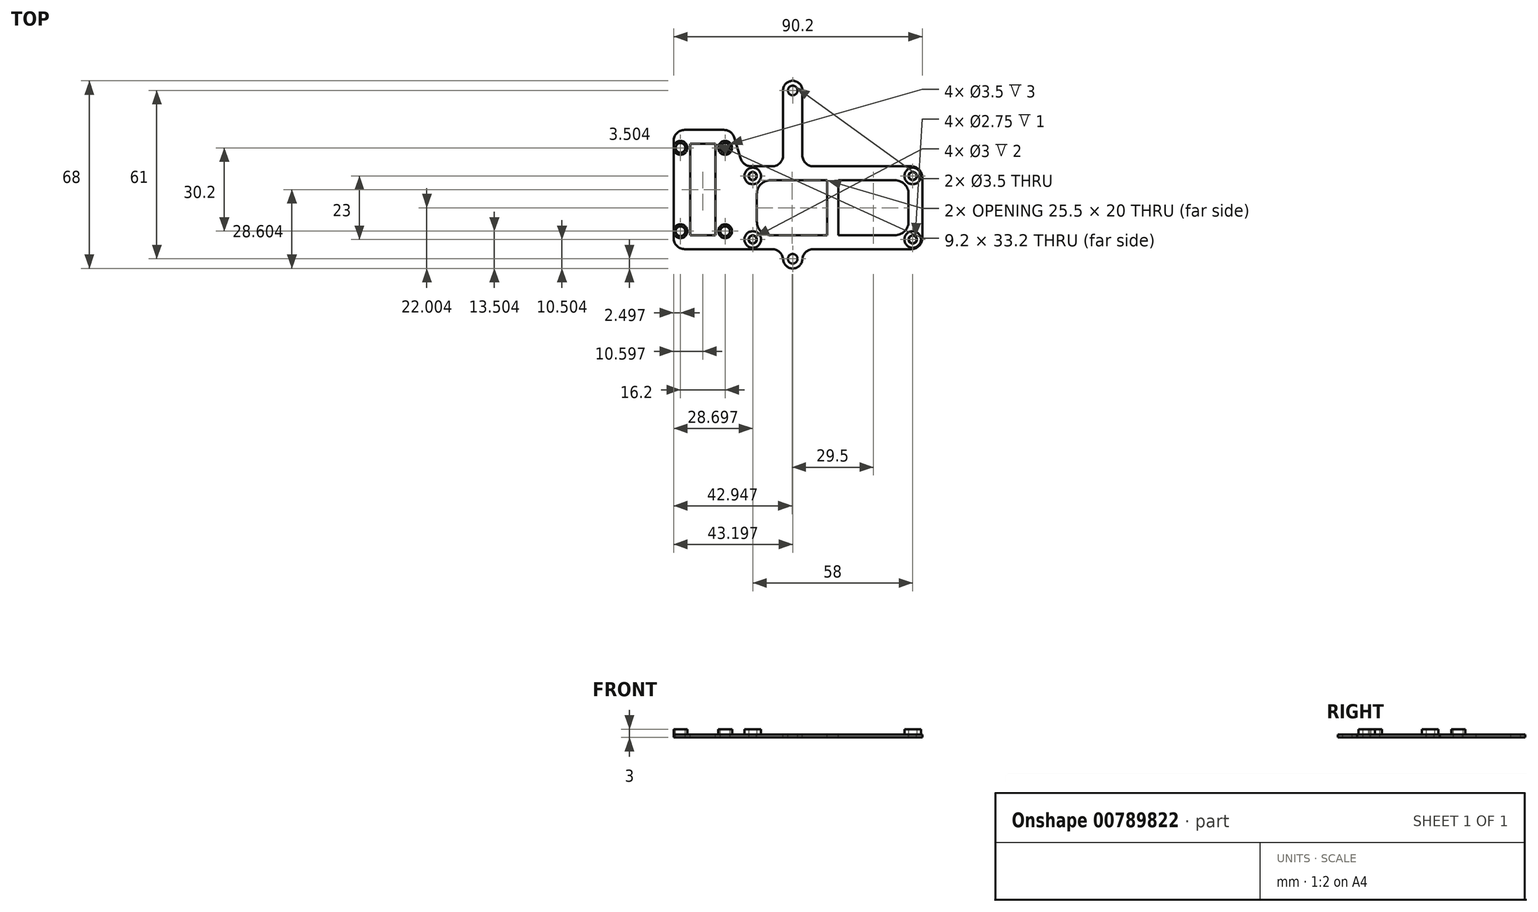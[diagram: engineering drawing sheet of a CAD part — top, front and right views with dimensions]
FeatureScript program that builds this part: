
annotation { "Feature Type Name" : "Feature", "Feature Type Description" : "" }
export const myFeature = defineFeature(function(context is Context, id is Id, definition is map)
    precondition{}
    {
        {
            var Q0;
            Q0=qCreatedBy(makeId("Top.planeOp"),FACE);
            var sketch = newSketch(context, id + "F0", { "sketchPlane" : qUnion([Q0])});
            skLineSegment(sketch, "E0", {"start": v(-80.72, -19.29) * mm, "end": v(-39.23, -19.29) * mm, "construction": true});
            skLineSegment(sketch, "E1", {"start": v(-86.78, -69.8) * mm, "end": v(-86.78, 17.15) * mm, "construction": true});
            skLineSegment(sketch, "E2.bottom", {"start": v(-119.28, -4.29) * mm, "end": v(-54.28, -4.29) * mm});
            skLineSegment(sketch, "E2.top", {"start": v(-119.28, -34.29) * mm, "end": v(-54.28, -34.29) * mm});
            skLineSegment(sketch, "E2.left", {"start": v(-119.28, -4.29) * mm, "end": v(-119.28, -34.29) * mm});
            skLineSegment(sketch, "E2.right", {"start": v(-54.28, -4.29) * mm, "end": v(-54.28, -34.29) * mm});
            skCircle(sketch, "E3", {"center": v(-57.78, -7.79) * mm, "radius": 1.38 * mm});
            skCircle(sketch, "E4.MirrorC", {"center": v(-115.78, -7.79) * mm, "radius": 1.38 * mm});
            skCircle(sketch, "E5.MirrorC", {"center": v(-57.78, -30.79) * mm, "radius": 1.38 * mm});
            skCircle(sketch, "E6.MirrorC", {"center": v(-115.78, -30.79) * mm, "radius": 1.38 * mm});
            skLineSegment(sketch, "E7.bottom", {"start": v(-59.28, -14.29) * mm, "end": v(-59.28, -24.29) * mm});
            skLineSegment(sketch, "E7.top", {"start": v(-84.78, -9.29) * mm, "end": v(-84.78, -29.29) * mm});
            skLineSegment(sketch, "E7.left", {"start": v(-64.28, -9.29) * mm, "end": v(-84.78, -9.29) * mm});
            skLineSegment(sketch, "E7.right", {"start": v(-64.28, -29.29) * mm, "end": v(-84.78, -29.29) * mm});
            skLineSegment(sketch, "E8.MirrorCS", {"start": v(-109.28, -9.29) * mm, "end": v(-88.78, -9.29) * mm});
            skLineSegment(sketch, "E9.MirrorCS", {"start": v(-114.28, -14.29) * mm, "end": v(-114.28, -24.29) * mm});
            skLineSegment(sketch, "E10.MirrorCS", {"start": v(-109.28, -29.29) * mm, "end": v(-88.78, -29.29) * mm});
            skLineSegment(sketch, "E11.MirrorCS", {"start": v(-88.78, -9.29) * mm, "end": v(-88.78, -29.29) * mm});
            skPoint(sketch, "E12.visualSharp", {"position": v(-59.28, -9.29) * mm});
            skArc(sketch, "E12.filletArc", {"start": v(-59.28, -14.29) * mm, "mid": v(-60.75, -10.75) * mm, "end": v(-64.28, -9.29) * mm});
            skPoint(sketch, "E13.visualSharp", {"position": v(-59.28, -29.29) * mm});
            skArc(sketch, "E13.filletArc", {"start": v(-64.28, -29.29) * mm, "mid": v(-60.75, -27.82) * mm, "end": v(-59.28, -24.29) * mm});
            skPoint(sketch, "E14.visualSharp", {"position": v(-114.28, -9.29) * mm});
            skArc(sketch, "E14.filletArc", {"start": v(-109.28, -9.29) * mm, "mid": v(-112.82, -10.75) * mm, "end": v(-114.28, -14.29) * mm});
            skPoint(sketch, "E15.visualSharp", {"position": v(-114.28, -29.29) * mm});
            skArc(sketch, "E15.filletArc", {"start": v(-114.28, -24.29) * mm, "mid": v(-112.82, -27.82) * mm, "end": v(-109.28, -29.29) * mm});
            skLineSegment(sketch, "E16.bottom", {"start": v(-144.48, 8.91) * mm, "end": v(-123.28, 8.91) * mm});
            skLineSegment(sketch, "E16.top", {"start": v(-144.48, -34.29) * mm, "end": v(-123.28, -34.29) * mm});
            skLineSegment(sketch, "E16.left", {"start": v(-144.48, 8.91) * mm, "end": v(-144.48, -34.29) * mm});
            skLineSegment(sketch, "E16.right", {"start": v(-123.28, 8.91) * mm, "end": v(-123.28, -34.29) * mm});
            skCircle(sketch, "E17", {"center": v(-141.98, 2.41) * mm, "radius": 1.75 * mm});
            skLineSegment(sketch, "E18.bottom", {"start": v(-138.48, 3.91) * mm, "end": v(-129.28, 3.91) * mm});
            skLineSegment(sketch, "E18.top", {"start": v(-138.48, -29.29) * mm, "end": v(-129.28, -29.29) * mm});
            skLineSegment(sketch, "E18.left", {"start": v(-138.48, 3.91) * mm, "end": v(-138.48, -29.29) * mm});
            skLineSegment(sketch, "E18.right", {"start": v(-129.28, 3.91) * mm, "end": v(-129.28, -29.29) * mm});
            skLineSegment(sketch, "E19", {"start": v(-133.88, 7.5) * mm, "end": v(-133.88, -46.86) * mm, "construction": true});
            skLineSegment(sketch, "E20", {"start": v(-113.33, -12.69) * mm, "end": v(-148.45, -12.69) * mm, "construction": true});
            skCircle(sketch, "E21.MirrorC", {"center": v(-125.78, 2.41) * mm, "radius": 1.75 * mm});
            skCircle(sketch, "E22.MirrorC", {"center": v(-141.98, -27.79) * mm, "radius": 1.75 * mm});
            skCircle(sketch, "E23.MirrorC", {"center": v(-125.78, -27.79) * mm, "radius": 1.75 * mm});
            skCircle(sketch, "E24", {"center": v(-101.28, 23.21) * mm, "radius": 1.75 * mm});
            skCircle(sketch, "E25", {"center": v(-101.28, -37.79) * mm, "radius": 1.75 * mm});
            skLineSegment(sketch, "E26", {"start": v(-101.28, 33.32) * mm, "end": v(-101.28, -52.86) * mm, "construction": true});
            skCircle(sketch, "E27", {"center": v(-101.28, 23.21) * mm, "radius": 3.5 * mm, "construction": true});
            skCircle(sketch, "E28", {"center": v(-101.28, -37.79) * mm, "radius": 3.5 * mm, "construction": true});
            skLineSegment(sketch, "E29", {"start": v(-176.77, -34.29) * mm, "end": v(-12.88, -34.29) * mm, "construction": true});
            skLineSegment(sketch, "E30", {"start": v(-104.78, 23.21) * mm, "end": v(-104.78, -44.28) * mm});
            skLineSegment(sketch, "E31", {"start": v(-97.78, 23.21) * mm, "end": v(-97.78, -43.09) * mm});
            skArc(sketch, "E32", {"start": v(-97.78, 23.21) * mm, "mid": v(-101.28, 26.71) * mm, "end": v(-104.78, 23.21) * mm});
            skArc(sketch, "E33", {"start": v(-97.78, -37.79) * mm, "mid": v(-101.28, -41.29) * mm, "end": v(-104.78, -37.79) * mm});
            skLineSegment(sketch, "E34", {"start": v(-123.28, 8.91) * mm, "end": v(-119.28, -4.29) * mm});
            skLineSegment(sketch, "E35", {"start": v(-123.28, -34.29) * mm, "end": v(-119.28, -34.29) * mm});
            skSolve(sketch);
        }
        {
            var Q0;
            Q0=qCreatedBy(makeId("Top.planeOp"),FACE);
            var sketch = newSketch(context, id + "F1", { "sketchPlane" : qUnion([Q0])});
            skCircle(sketch, "E36", {"center": v(-115.78, -7.79) * mm, "radius": 1.5 * mm});
            skCircle(sketch, "E37", {"center": v(-115.78, -7.79) * mm, "radius": 3 * mm});
            skCircle(sketch, "E38.MirrorC", {"center": v(-115.78, -30.79) * mm, "radius": 3 * mm});
            skCircle(sketch, "E39.MirrorC", {"center": v(-115.78, -30.79) * mm, "radius": 1.5 * mm});
            skCircle(sketch, "E40.MirrorC", {"center": v(-57.78, -7.79) * mm, "radius": 1.5 * mm});
            skCircle(sketch, "E41.MirrorC", {"center": v(-57.78, -7.79) * mm, "radius": 3 * mm});
            skCircle(sketch, "E42.MirrorC", {"center": v(-57.78, -30.79) * mm, "radius": 3 * mm});
            skCircle(sketch, "E43.MirrorC", {"center": v(-57.78, -30.79) * mm, "radius": 1.5 * mm});
            skCircle(sketch, "E44", {"center": v(-141.98, 2.41) * mm, "radius": 2.5 * mm});
            skCircle(sketch, "E45.MirrorC", {"center": v(-141.98, -27.79) * mm, "radius": 2.5 * mm});
            skCircle(sketch, "E46.MirrorC", {"center": v(-125.78, 2.41) * mm, "radius": 2.5 * mm});
            skCircle(sketch, "E47.MirrorC", {"center": v(-125.78, -27.79) * mm, "radius": 2.5 * mm});
            skCircle(sketch, "E48", {"center": v(-141.98, 2.41) * mm, "radius": 1.75 * mm});
            skCircle(sketch, "E49.MirrorC", {"center": v(-125.78, 2.41) * mm, "radius": 1.75 * mm});
            skCircle(sketch, "E50.MirrorC", {"center": v(-141.98, -27.79) * mm, "radius": 1.75 * mm});
            skCircle(sketch, "E51.MirrorC", {"center": v(-125.78, -27.79) * mm, "radius": 1.75 * mm});
            skSolve(sketch);
        }
        {
            var Q0;
            Q0 = qSketchRegion(id + "F0", true);
            extrude(context, id + "F2", {"entities" : qUnion([Q0]), "oppositeDirection" : true, "depth" : 1 * mm, "offsetDistance" : 25 * mm});
        }
        {
            var Q0;
            Q0 = qSketchRegion(id + "F1", true);
            extrude(context, id + "F3", {"entities" : qUnion([Q0]), "operationType" : NewBodyOperationType.ADD, "depth" : 2 * mm, "offsetDistance" : 25 * mm});
        }
        {
            var Q0;
            Q0=makeQuery(id+"F2.opExtrude","SWEPT_EDGE",EDGE,{"disambiguationData":[OSD([sQuery(id+"F0.wireOp",EDGE,"E16.bottom"),sQuery(id+"F0.wireOp",EDGE,"E16.left")])]});
            var Q1;
            Q1=makeQuery(id+"F2.opExtrude","SWEPT_EDGE",EDGE,{"disambiguationData":[OSD([sQuery(id+"F0.wireOp",EDGE,"E16.bottom"),sQuery(id+"F0.wireOp",EDGE,"E16.right"),sQuery(id+"F0.wireOp",EDGE,"E34")])]});
            var Q2;
            Q2=makeQuery(id+"F2.opExtrude","SWEPT_EDGE",EDGE,{"disambiguationData":[OSD([sQuery(id+"F0.wireOp",EDGE,"E2.bottom"),sQuery(id+"F0.wireOp",EDGE,"E2.left"),sQuery(id+"F0.wireOp",EDGE,"E34")])]});
            var Q3;
            Q3=makeQuery(id+"F2.opExtrude","SWEPT_EDGE",EDGE,{"disambiguationData":[OSD([sQuery(id+"F0.wireOp",EDGE,"E2.bottom"),sQuery(id+"F0.wireOp",EDGE,"E2.right")])]});
            var Q4;
            Q4=makeQuery(id+"F2.opExtrude","SWEPT_EDGE",EDGE,{"disambiguationData":[OSD([sQuery(id+"F0.wireOp",EDGE,"E2.bottom"),sQuery(id+"F0.wireOp",EDGE,"E31")])]});
            var Q5;
            Q5=makeQuery(id+"F2.opExtrude","SWEPT_EDGE",EDGE,{"disambiguationData":[OSD([sQuery(id+"F0.wireOp",EDGE,"E2.bottom"),sQuery(id+"F0.wireOp",EDGE,"E30")])]});
            var Q6;
            Q6=makeQuery(id+"F2.opExtrude","SWEPT_EDGE",EDGE,{"disambiguationData":[OSD([sQuery(id+"F0.wireOp",EDGE,"E16.top"),sQuery(id+"F0.wireOp",EDGE,"E16.left")])]});
            var Q7;
            Q7=makeQuery(id+"F2.opExtrude","SWEPT_EDGE",EDGE,{"disambiguationData":[OSD([sQuery(id+"F0.wireOp",EDGE,"E2.top"),sQuery(id+"F0.wireOp",EDGE,"E2.right")])]});
            var Q8;
            Q8=makeQuery(id+"F2.opExtrude","SWEPT_EDGE",EDGE,{"disambiguationData":[OSD([sQuery(id+"F0.wireOp",EDGE,"E2.top"),sQuery(id+"F0.wireOp",EDGE,"E31")])]});
            var Q9;
            Q9=makeQuery(id+"F2.opExtrude","SWEPT_EDGE",EDGE,{"disambiguationData":[OSD([sQuery(id+"F0.wireOp",EDGE,"E2.top"),sQuery(id+"F0.wireOp",EDGE,"E30")])]});
            fillet(context, id + "F4", {"entities" : qUnion([Q0, Q1, Q2, Q3, Q4, Q5, Q6, Q7, Q8, Q9]), "radius" : 4 * mm, "tangentPropagation" : true, "allowEdgeOverflow" : false});
        }
    });
